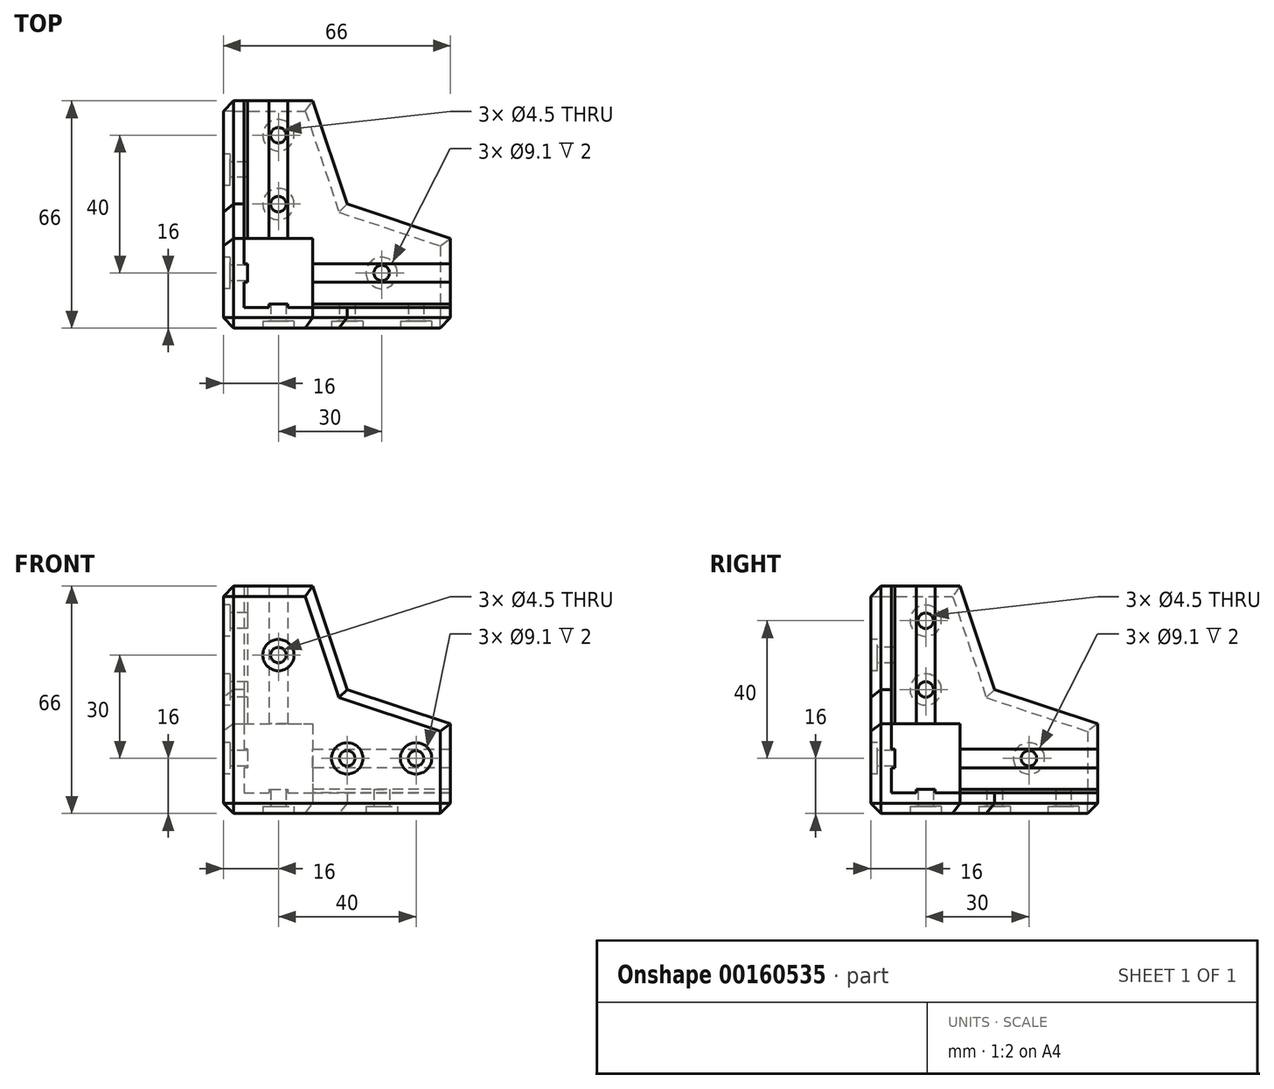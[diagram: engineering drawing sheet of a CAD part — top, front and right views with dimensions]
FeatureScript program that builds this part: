
annotation { "Feature Type Name" : "Feature", "Feature Type Description" : "" }
export const myFeature = defineFeature(function(context is Context, id is Id, definition is map)
    precondition{}
    {
        {
            var Q0;
            Q0=qCreatedBy(makeId("Top.planeOp"),FACE);
            var sketch = newSketch(context, id + "F0", { "sketchPlane" : qUnion([Q0])});
            skLineSegment(sketch, "E0", {"start": v(0, 0) * mm, "end": v(0, 66) * mm});
            skLineSegment(sketch, "E1", {"start": v(0, 66) * mm, "end": v(26, 66) * mm});
            skLineSegment(sketch, "E2", {"start": v(26, 66) * mm, "end": v(26, 26) * mm});
            skLineSegment(sketch, "E3", {"start": v(26, 26) * mm, "end": v(66, 26) * mm});
            skLineSegment(sketch, "E4", {"start": v(66, 26) * mm, "end": v(66, 0) * mm});
            skLineSegment(sketch, "E5", {"start": v(66, 0) * mm, "end": v(0, 0) * mm});
            skLineSegment(sketch, "E6", {"start": v(66, 6) * mm, "end": v(6, 6) * mm, "construction": true});
            skLineSegment(sketch, "E7", {"start": v(6, 6) * mm, "end": v(6, 66) * mm, "construction": true});
            skSolve(sketch);
        }
        {
            var Q0;
            Q0=qSketchRegion(id+"F0",true);
            extrude(context, id + "F1", {"entities" : qUnion([Q0]), "depth" : 6 * mm});
        }
        {
            var Q0;
            Q0=makeQuery(id+"F1.opExtrude","CAP_FACE",FACE,{"disambiguationData":[OSD([sQuery(id+"F0.wireOp",EDGE,"E0"),sQuery(id+"F0.wireOp",EDGE,"E1"),sQuery(id+"F0.wireOp",EDGE,"E2"),sQuery(id+"F0.wireOp",EDGE,"E3"),sQuery(id+"F0.wireOp",EDGE,"E4"),sQuery(id+"F0.wireOp",EDGE,"E5")])],"isStart":false});
            var sketch = newSketch(context, id + "F2", { "sketchPlane" : qUnion([Q0])});
            skLineSegment(sketch, "E8", {"start": v(0, 66) * mm, "end": v(6, 66) * mm});
            skLineSegment(sketch, "E9", {"start": v(6, 66) * mm, "end": v(6, 6) * mm});
            skLineSegment(sketch, "E10", {"start": v(6, 6) * mm, "end": v(66, 6) * mm});
            skLineSegment(sketch, "E11", {"start": v(66, 6) * mm, "end": v(66, 0) * mm});
            skLineSegment(sketch, "E12", {"start": v(66, 0) * mm, "end": v(0, 0) * mm});
            skLineSegment(sketch, "E13", {"start": v(0, 0) * mm, "end": v(0, 66) * mm});
            skSolve(sketch);
        }
        {
            var Q0;
            Q0=makeQuery(id+"F2.imprint","IMPRINT",FACE,{"disambiguationData":[TD([[makeQuery(id+"F2.imprint","IMPRINT",EDGE,{"derivedFrom":sQuery(id+"F2.wireOp",EDGE,"E8")}),-1.0]])]});
            extrude(context, id + "F3", {"entities" : qUnion([Q0]), "operationType" : NewBodyOperationType.ADD, "depth" : 20 * mm});
        }
        {
            var Q0;
            Q0=makeQuery(id+"F3.opExtrude","CAP_FACE",FACE,{"disambiguationData":[OSD([sQuery(id+"F2.wireOp",EDGE,"E8"),sQuery(id+"F2.wireOp",EDGE,"E9"),sQuery(id+"F2.wireOp",EDGE,"E10"),sQuery(id+"F2.wireOp",EDGE,"E11"),sQuery(id+"F2.wireOp",EDGE,"E12"),sQuery(id+"F2.wireOp",EDGE,"E13")])],"isStart":false});
            var sketch = newSketch(context, id + "F4", { "sketchPlane" : qUnion([Q0])});
            skLineSegment(sketch, "E14", {"start": v(6, 26) * mm, "end": v(0, 26) * mm});
            skLineSegment(sketch, "E15", {"start": v(0, 26) * mm, "end": v(0, 0) * mm});
            skLineSegment(sketch, "E16", {"start": v(0, 0) * mm, "end": v(26, 0) * mm});
            skLineSegment(sketch, "E17", {"start": v(26, 0) * mm, "end": v(26, 6) * mm});
            skLineSegment(sketch, "E18", {"start": v(26, 6) * mm, "end": v(6, 6) * mm});
            skLineSegment(sketch, "E19", {"start": v(6, 6) * mm, "end": v(6, 26) * mm});
            skSolve(sketch);
        }
        {
            var Q0;
            Q0=qSketchRegion(id+"F4",true);
            extrude(context, id + "F5", {"entities" : qUnion([Q0]), "operationType" : NewBodyOperationType.ADD, "depth" : 40 * mm});
        }
        {
            var Q0;
            Q0=makeQuery(id+"F1.opExtrude","CAP_FACE",FACE,{"disambiguationData":[OSD([sQuery(id+"F0.wireOp",EDGE,"E0"),sQuery(id+"F0.wireOp",EDGE,"E1"),sQuery(id+"F0.wireOp",EDGE,"E2"),sQuery(id+"F0.wireOp",EDGE,"E3"),sQuery(id+"F0.wireOp",EDGE,"E4"),sQuery(id+"F0.wireOp",EDGE,"E5")])],"isStart":false});
            var sketch = newSketch(context, id + "F6", { "sketchPlane" : qUnion([Q0])});
            skLineSegment(sketch, "E20", {"start": v(66, 16) * mm, "end": v(6, 16) * mm, "construction": true});
            skLineSegment(sketch, "E21", {"start": v(16, 66) * mm, "end": v(16, 6) * mm, "construction": true});
            skLineSegment(sketch, "E22", {"start": v(16, 6) * mm, "end": v(18.71, 6) * mm});
            skLineSegment(sketch, "E23", {"start": v(18.71, 6) * mm, "end": v(18.71, 7) * mm});
            skLineSegment(sketch, "E24", {"start": v(18.71, 7) * mm, "end": v(13.3, 7) * mm});
            skLineSegment(sketch, "E25", {"start": v(13.3, 7) * mm, "end": v(13.3, 6) * mm});
            skLineSegment(sketch, "E26", {"start": v(13.3, 6) * mm, "end": v(16, 6) * mm});
            skLineSegment(sketch, "E27", {"start": v(6, 16) * mm, "end": v(6, 18.7) * mm});
            skLineSegment(sketch, "E28", {"start": v(6, 18.7) * mm, "end": v(7, 18.7) * mm});
            skLineSegment(sketch, "E29", {"start": v(7, 18.7) * mm, "end": v(7, 13.29) * mm});
            skLineSegment(sketch, "E30", {"start": v(7, 13.29) * mm, "end": v(6, 13.29) * mm});
            skLineSegment(sketch, "E31", {"start": v(6, 13.29) * mm, "end": v(6, 16) * mm});
            skSolve(sketch);
        }
        {
            var Q0;
            Q0=qSketchRegion(id+"F6",true);
            extrude(context, id + "F7", {"entities" : qUnion([Q0]), "operationType" : NewBodyOperationType.ADD, "depth" : 60 * mm});
        }
        {
            var Q0;
            Q0=makeQuery(id+"F1.opExtrude","CAP_FACE",FACE,{"disambiguationData":[OSD([sQuery(id+"F0.wireOp",EDGE,"E0"),sQuery(id+"F0.wireOp",EDGE,"E1"),sQuery(id+"F0.wireOp",EDGE,"E2"),sQuery(id+"F0.wireOp",EDGE,"E3"),sQuery(id+"F0.wireOp",EDGE,"E4"),sQuery(id+"F0.wireOp",EDGE,"E5")])],"isStart":false});
            var sketch = newSketch(context, id + "F8", { "sketchPlane" : qUnion([Q0])});
            skLineSegment(sketch, "E32", {"start": v(66, 16) * mm, "end": v(7, 16) * mm, "construction": true});
            skLineSegment(sketch, "E33", {"start": v(66, 16) * mm, "end": v(66, 18.7) * mm});
            skLineSegment(sketch, "E34", {"start": v(66, 18.7) * mm, "end": v(26, 18.7) * mm});
            skLineSegment(sketch, "E35", {"start": v(26, 18.7) * mm, "end": v(26, 13.29) * mm});
            skLineSegment(sketch, "E36", {"start": v(26, 13.29) * mm, "end": v(66, 13.29) * mm});
            skLineSegment(sketch, "E37", {"start": v(66, 13.29) * mm, "end": v(66, 16) * mm});
            skLineSegment(sketch, "E38", {"start": v(16, 66) * mm, "end": v(16, 7) * mm, "construction": true});
            skLineSegment(sketch, "E39", {"start": v(16, 66) * mm, "end": v(13.3, 66) * mm});
            skLineSegment(sketch, "E40", {"start": v(13.3, 66) * mm, "end": v(13.3, 26) * mm});
            skLineSegment(sketch, "E41", {"start": v(13.3, 26) * mm, "end": v(18.7, 26) * mm});
            skLineSegment(sketch, "E42", {"start": v(18.7, 26) * mm, "end": v(18.7, 66) * mm});
            skLineSegment(sketch, "E43", {"start": v(18.7, 66) * mm, "end": v(16, 66) * mm});
            skSolve(sketch);
        }
        {
            var Q0;
            Q0=qSketchRegion(id+"F8",true);
            extrude(context, id + "F9", {"entities" : qUnion([Q0]), "operationType" : NewBodyOperationType.ADD, "flatOperationType" : FlatOperationType.REMOVE, "offsetDistance" : 25 * mm, "depth" : 1 * mm, "domain" : OperationDomain.MODEL});
        }
        {
            var Q0;
            {var subQ1=sQuery(id+"F2.wireOp",EDGE,"E10");var subQ2=sQuery(id+"F0.wireOp",EDGE,"E4");var subQ3=sQuery(id+"F4.wireOp",EDGE,"E18");Q0=makeQuery(id+"F7.boolean.opBoolean","SPLIT",FACE,{"disambiguationData":[TD([makeQuery(id+"F1.opExtrude","SWEPT_FACE",FACE,{"disambiguationData":[OSD([subQ2])]})])],"derivedFrom":makeQuery(id+"F5.boolean.opBoolean","MERGE",FACE,{"derivedFrom":[makeQuery(id+"F3.opExtrude","SWEPT_FACE",FACE,{"disambiguationData":[OSD([subQ1])]}),makeQuery(id+"F5.opExtrude","SWEPT_FACE",FACE,{"disambiguationData":[OSD([subQ3])]})]})});}
            var sketch = newSketch(context, id + "F10", { "sketchPlane" : qUnion([Q0])});
            skLineSegment(sketch, "E44", {"start": v(-66, 16) * mm, "end": v(-26, 16) * mm, "construction": true});
            skLineSegment(sketch, "E45", {"start": v(-66, 16) * mm, "end": v(-66, 13.3) * mm});
            skLineSegment(sketch, "E46", {"start": v(-66, 13.3) * mm, "end": v(-26, 13.3) * mm});
            skLineSegment(sketch, "E47", {"start": v(-26, 13.3) * mm, "end": v(-26, 16) * mm});
            skLineSegment(sketch, "E48", {"start": v(-26, 18.71) * mm, "end": v(-66, 18.71) * mm});
            skLineSegment(sketch, "E49", {"start": v(-66, 18.71) * mm, "end": v(-66, 16) * mm});
            skLineSegment(sketch, "E50", {"start": v(-26, 18.71) * mm, "end": v(-26, 16) * mm});
            skSolve(sketch);
        }
        {
            var Q0;
            Q0=qSketchRegion(id+"F10",true);
            extrude(context, id + "F11", {"entities" : qUnion([Q0]), "operationType" : NewBodyOperationType.ADD, "flatOperationType" : FlatOperationType.REMOVE, "offsetDistance" : 25 * mm, "depth" : 1 * mm, "domain" : OperationDomain.MODEL});
        }
        {
            var Q0;
            {var subQ0=sQuery(id+"F2.wireOp",EDGE,"E9");var subQ3=sQuery(id+"F0.wireOp",EDGE,"E1");var subQ5=sQuery(id+"F4.wireOp",EDGE,"E19");Q0=makeQuery(id+"F7.boolean.opBoolean","SPLIT",FACE,{"disambiguationData":[TD([makeQuery(id+"F1.opExtrude","SWEPT_FACE",FACE,{"disambiguationData":[OSD([subQ3])]})])],"derivedFrom":makeQuery(id+"F5.boolean.opBoolean","MERGE",FACE,{"derivedFrom":[makeQuery(id+"F3.opExtrude","SWEPT_FACE",FACE,{"disambiguationData":[OSD([subQ0])]}),makeQuery(id+"F5.opExtrude","SWEPT_FACE",FACE,{"disambiguationData":[OSD([subQ5])]})]})});}
            var sketch = newSketch(context, id + "F12", { "sketchPlane" : qUnion([Q0])});
            skLineSegment(sketch, "E51", {"start": v(66, 16) * mm, "end": v(26, 16) * mm, "construction": true});
            skLineSegment(sketch, "E52", {"start": v(66, 16) * mm, "end": v(66, 18.71) * mm});
            skLineSegment(sketch, "E53", {"start": v(66, 18.71) * mm, "end": v(26, 18.7) * mm});
            skLineSegment(sketch, "E54", {"start": v(26, 18.7) * mm, "end": v(26, 13.29) * mm});
            skLineSegment(sketch, "E55", {"start": v(26, 13.29) * mm, "end": v(66, 13.29) * mm});
            skLineSegment(sketch, "E56", {"start": v(66, 16) * mm, "end": v(66, 13.29) * mm});
            skSolve(sketch);
        }
        {
            var Q0;
            Q0=qSketchRegion(id+"F12",true);
            extrude(context, id + "F13", {"entities" : qUnion([Q0]), "operationType" : NewBodyOperationType.ADD, "flatOperationType" : FlatOperationType.REMOVE, "offsetDistance" : 25 * mm, "depth" : 1 * mm, "domain" : OperationDomain.MODEL});
        }
        {
            var Q0;
            Q0=makeQuery(id+"F5.boolean.opBoolean","MERGE",FACE,{"derivedFrom":[makeQuery(id+"F3.boolean.opBoolean","MERGE",FACE,{"derivedFrom":[makeQuery(id+"F1.opExtrude","SWEPT_FACE",FACE,{"disambiguationData":[OSD([sQuery(id+"F0.wireOp",EDGE,"E5")])]}),makeQuery(id+"F3.opExtrude","SWEPT_FACE",FACE,{"disambiguationData":[OSD([sQuery(id+"F2.wireOp",EDGE,"E12")])]})]}),makeQuery(id+"F5.opExtrude","SWEPT_FACE",FACE,{"disambiguationData":[OSD([sQuery(id+"F4.wireOp",EDGE,"E16")])]})]});
            var sketch = newSketch(context, id + "F14", { "sketchPlane" : qUnion([Q0])});
            skLineSegment(sketch, "E57", {"start": v(6, 66) * mm, "end": v(6, 6) * mm, "construction": true});
            skLineSegment(sketch, "E58", {"start": v(6, 6) * mm, "end": v(66, 6) * mm, "construction": true});
            skCircle(sketch, "E59", {"center": v(56, 16) * mm, "radius": 2.25 * mm});
            skCircle(sketch, "E60", {"center": v(36, 16) * mm, "radius": 2.25 * mm});
            skCircle(sketch, "E61", {"center": v(16, 46) * mm, "radius": 2.25 * mm});
            skLineSegment(sketch, "E62", {"start": v(26, 26) * mm, "end": v(6, 26) * mm, "construction": true});
            skLineSegment(sketch, "E63", {"start": v(26, 26) * mm, "end": v(26, 6) * mm, "construction": true});
            skSolve(sketch);
        }
        {
            var Q0;
            Q0=makeQuery(id+"F14.imprint","IMPRINT",FACE,{"disambiguationData":[TD([[makeQuery(id+"F14.imprint","IMPRINT",EDGE,{"derivedFrom":sQuery(id+"F14.wireOp",EDGE,"E59")}),1.0]])]});
            var Q1;
            Q1=makeQuery(id+"F14.imprint","IMPRINT",FACE,{"disambiguationData":[TD([[makeQuery(id+"F14.imprint","IMPRINT",EDGE,{"derivedFrom":sQuery(id+"F14.wireOp",EDGE,"E61")}),1.0]])]});
            var Q2;
            Q2=makeQuery(id+"F14.imprint","IMPRINT",FACE,{"disambiguationData":[TD([[makeQuery(id+"F14.imprint","IMPRINT",EDGE,{"derivedFrom":sQuery(id+"F14.wireOp",EDGE,"E60")}),1.0]])]});
            extrude(context, id + "F15", {"entities" : qUnion([Q0, Q1, Q2]), "operationType" : NewBodyOperationType.REMOVE, "endBound" : BoundingType.UP_TO_NEXT, "oppositeDirection" : true, "depth" : 25 * mm});
        }
        {
            var Q0;
            Q0=makeQuery(id+"F5.boolean.opBoolean","MERGE",FACE,{"derivedFrom":[makeQuery(id+"F3.boolean.opBoolean","MERGE",FACE,{"derivedFrom":[makeQuery(id+"F1.opExtrude","SWEPT_FACE",FACE,{"disambiguationData":[OSD([sQuery(id+"F0.wireOp",EDGE,"E0")])]}),makeQuery(id+"F3.opExtrude","SWEPT_FACE",FACE,{"disambiguationData":[OSD([sQuery(id+"F2.wireOp",EDGE,"E13")])]})]}),makeQuery(id+"F5.opExtrude","SWEPT_FACE",FACE,{"disambiguationData":[OSD([sQuery(id+"F4.wireOp",EDGE,"E15")])]})]});
            var sketch = newSketch(context, id + "F16", { "sketchPlane" : qUnion([Q0])});
            skLineSegment(sketch, "E64", {"start": v(-6, 66) * mm, "end": v(-6, 6) * mm, "construction": true});
            skLineSegment(sketch, "E65", {"start": v(-6, 6) * mm, "end": v(-66, 6) * mm, "construction": true});
            skCircle(sketch, "E66", {"center": v(-16, 56) * mm, "radius": 2.25 * mm});
            skCircle(sketch, "E67", {"center": v(-46, 16) * mm, "radius": 2.25 * mm});
            skCircle(sketch, "E68", {"center": v(-16, 36) * mm, "radius": 2.25 * mm});
            skSolve(sketch);
        }
        {
            var Q0;
            Q0=qSketchRegion(id+"F16",true);
            extrude(context, id + "F17", {"entities" : qUnion([Q0]), "operationType" : NewBodyOperationType.REMOVE, "endBound" : BoundingType.UP_TO_NEXT, "oppositeDirection" : true, "depth" : 25 * mm});
        }
        {
            var Q0;
            Q0=makeQuery(id+"F1.opExtrude","CAP_FACE",FACE,{"disambiguationData":[OSD([sQuery(id+"F0.wireOp",EDGE,"E0"),sQuery(id+"F0.wireOp",EDGE,"E1"),sQuery(id+"F0.wireOp",EDGE,"E2"),sQuery(id+"F0.wireOp",EDGE,"E3"),sQuery(id+"F0.wireOp",EDGE,"E4"),sQuery(id+"F0.wireOp",EDGE,"E5")])],"isStart":true});
            var sketch = newSketch(context, id + "F18", { "sketchPlane" : qUnion([Q0])});
            skLineSegment(sketch, "E69", {"start": v(66, -6) * mm, "end": v(6, -6) * mm, "construction": true});
            skLineSegment(sketch, "E70", {"start": v(6, -6) * mm, "end": v(6, -66) * mm, "construction": true});
            skCircle(sketch, "E71", {"center": v(46, -16) * mm, "radius": 2.25 * mm});
            skCircle(sketch, "E72", {"center": v(16, -56) * mm, "radius": 2.25 * mm});
            skCircle(sketch, "E73", {"center": v(16, -36) * mm, "radius": 2.25 * mm});
            skSolve(sketch);
        }
        {
            var Q0;
            Q0=qSketchRegion(id+"F18",true);
            extrude(context, id + "F19", {"entities" : qUnion([Q0]), "operationType" : NewBodyOperationType.REMOVE, "endBound" : BoundingType.UP_TO_NEXT, "oppositeDirection" : true, "depth" : 25 * mm});
        }
        {
            var Q0;
            Q0=makeQuery(id+"F5.boolean.opBoolean","MERGE",FACE,{"derivedFrom":[makeQuery(id+"F3.boolean.opBoolean","MERGE",FACE,{"derivedFrom":[makeQuery(id+"F1.opExtrude","SWEPT_FACE",FACE,{"disambiguationData":[OSD([sQuery(id+"F0.wireOp",EDGE,"E5")])]}),makeQuery(id+"F3.opExtrude","SWEPT_FACE",FACE,{"disambiguationData":[OSD([sQuery(id+"F2.wireOp",EDGE,"E12")])]})]}),makeQuery(id+"F5.opExtrude","SWEPT_FACE",FACE,{"disambiguationData":[OSD([sQuery(id+"F4.wireOp",EDGE,"E16")])]})]});
            var sketch = newSketch(context, id + "F20", { "sketchPlane" : qUnion([Q0])});
            skCircle(sketch, "E74", {"center": v(16, 46) * mm, "radius": 4.55 * mm});
            skCircle(sketch, "E75", {"center": v(36, 16) * mm, "radius": 4.55 * mm});
            skCircle(sketch, "E76", {"center": v(56, 16) * mm, "radius": 4.55 * mm});
            skSolve(sketch);
        }
        {
            var Q0;
            Q0=qSketchRegion(id+"F20",true);
            extrude(context, id + "F21", {"entities" : qUnion([Q0]), "operationType" : NewBodyOperationType.REMOVE, "oppositeDirection" : true, "depth" : 2 * mm});
        }
        {
            var Q0;
            Q0=makeQuery(id+"F5.boolean.opBoolean","MERGE",FACE,{"derivedFrom":[makeQuery(id+"F3.boolean.opBoolean","MERGE",FACE,{"derivedFrom":[makeQuery(id+"F1.opExtrude","SWEPT_FACE",FACE,{"disambiguationData":[OSD([sQuery(id+"F0.wireOp",EDGE,"E0")])]}),makeQuery(id+"F3.opExtrude","SWEPT_FACE",FACE,{"disambiguationData":[OSD([sQuery(id+"F2.wireOp",EDGE,"E13")])]})]}),makeQuery(id+"F5.opExtrude","SWEPT_FACE",FACE,{"disambiguationData":[OSD([sQuery(id+"F4.wireOp",EDGE,"E15")])]})]});
            var sketch = newSketch(context, id + "F22", { "sketchPlane" : qUnion([Q0])});
            skCircle(sketch, "E77", {"center": v(-16, 56) * mm, "radius": 4.55 * mm});
            skCircle(sketch, "E78", {"center": v(-46, 16) * mm, "radius": 4.55 * mm});
            skCircle(sketch, "E79", {"center": v(-16, 36) * mm, "radius": 4.55 * mm});
            skSolve(sketch);
        }
        {
            var Q0;
            Q0=qSketchRegion(id+"F22",true);
            extrude(context, id + "F23", {"entities" : qUnion([Q0]), "operationType" : NewBodyOperationType.REMOVE, "oppositeDirection" : true, "depth" : 2 * mm});
        }
        {
            var Q0;
            Q0=makeQuery(id+"F1.opExtrude","CAP_FACE",FACE,{"disambiguationData":[OSD([sQuery(id+"F0.wireOp",EDGE,"E0"),sQuery(id+"F0.wireOp",EDGE,"E1"),sQuery(id+"F0.wireOp",EDGE,"E2"),sQuery(id+"F0.wireOp",EDGE,"E3"),sQuery(id+"F0.wireOp",EDGE,"E4"),sQuery(id+"F0.wireOp",EDGE,"E5")])],"isStart":true});
            var sketch = newSketch(context, id + "F24", { "sketchPlane" : qUnion([Q0])});
            skCircle(sketch, "E80", {"center": v(16, -56) * mm, "radius": 4.55 * mm});
            skCircle(sketch, "E81", {"center": v(46, -16) * mm, "radius": 4.55 * mm});
            skCircle(sketch, "E82", {"center": v(16, -36) * mm, "radius": 4.55 * mm});
            skSolve(sketch);
        }
        {
            var Q0;
            Q0=qSketchRegion(id+"F24",true);
            extrude(context, id + "F25", {"entities" : qUnion([Q0]), "operationType" : NewBodyOperationType.REMOVE, "oppositeDirection" : true, "depth" : 2 * mm});
        }
        {
            var Q0;
            Q0=makeQuery(id+"F1.opExtrude","CAP_FACE",FACE,{"disambiguationData":[OSD([sQuery(id+"F0.wireOp",EDGE,"E0"),sQuery(id+"F0.wireOp",EDGE,"E1"),sQuery(id+"F0.wireOp",EDGE,"E2"),sQuery(id+"F0.wireOp",EDGE,"E3"),sQuery(id+"F0.wireOp",EDGE,"E4"),sQuery(id+"F0.wireOp",EDGE,"E5")])],"isStart":false});
            var sketch = newSketch(context, id + "F26", { "sketchPlane" : qUnion([Q0])});
            skLineSegment(sketch, "E83.bottom", {"start": v(6, 6) * mm, "end": v(26, 6) * mm});
            skLineSegment(sketch, "E83.top", {"start": v(6, 26) * mm, "end": v(26, 26) * mm});
            skLineSegment(sketch, "E83.left", {"start": v(6, 6) * mm, "end": v(6, 26) * mm});
            skLineSegment(sketch, "E83.right", {"start": v(26, 6) * mm, "end": v(26, 26) * mm});
            skSolve(sketch);
        }
        {
            var Q0;
            Q0=qSketchRegion(id+"F26",true);
            extrude(context, id + "F27", {"entities" : qUnion([Q0]), "operationType" : NewBodyOperationType.ADD, "depth" : 20 * mm});
        }
        {
            var Q0;
            Q0=makeQuery(id+"F5.boolean.opBoolean","MERGE",FACE,{"derivedFrom":[makeQuery(id+"F3.boolean.opBoolean","MERGE",FACE,{"derivedFrom":[makeQuery(id+"F1.opExtrude","SWEPT_FACE",FACE,{"disambiguationData":[OSD([sQuery(id+"F0.wireOp",EDGE,"E5")])]}),makeQuery(id+"F3.opExtrude","SWEPT_FACE",FACE,{"disambiguationData":[OSD([sQuery(id+"F2.wireOp",EDGE,"E12")])]})]}),makeQuery(id+"F5.opExtrude","SWEPT_FACE",FACE,{"disambiguationData":[OSD([sQuery(id+"F4.wireOp",EDGE,"E16")])]})]});
            var sketch = newSketch(context, id + "F28", { "sketchPlane" : qUnion([Q0])});
            skLineSegment(sketch, "E84", {"start": v(26, 36) * mm, "end": v(36, 36) * mm, "construction": true});
            skLineSegment(sketch, "E85", {"start": v(36, 36) * mm, "end": v(36, 26) * mm, "construction": true});
            skLineSegment(sketch, "E86", {"start": v(26, 66) * mm, "end": v(36, 36) * mm});
            skLineSegment(sketch, "E87", {"start": v(36, 36) * mm, "end": v(66, 26) * mm});
            skLineSegment(sketch, "E88", {"start": v(66, 26) * mm, "end": v(26, 26) * mm});
            skLineSegment(sketch, "E89", {"start": v(26, 26) * mm, "end": v(26, 66) * mm});
            skSolve(sketch);
        }
        {
            var Q0;
            Q0 = qSketchRegion(id + "F28", true);
            extrude(context, id + "F29", {"entities" : qUnion([Q0]), "operationType" : NewBodyOperationType.ADD, "oppositeDirection" : true, "depth" : 6 * mm});
        }
        {
            var Q0;
            Q0=makeQuery(id+"F5.boolean.opBoolean","MERGE",FACE,{"derivedFrom":[makeQuery(id+"F3.boolean.opBoolean","MERGE",FACE,{"derivedFrom":[makeQuery(id+"F1.opExtrude","SWEPT_FACE",FACE,{"disambiguationData":[OSD([sQuery(id+"F0.wireOp",EDGE,"E0")])]}),makeQuery(id+"F3.opExtrude","SWEPT_FACE",FACE,{"disambiguationData":[OSD([sQuery(id+"F2.wireOp",EDGE,"E13")])]})]}),makeQuery(id+"F5.opExtrude","SWEPT_FACE",FACE,{"disambiguationData":[OSD([sQuery(id+"F4.wireOp",EDGE,"E15")])]})]});
            var sketch = newSketch(context, id + "F30", { "sketchPlane" : qUnion([Q0])});
            skLineSegment(sketch, "E90", {"start": v(-26, 36) * mm, "end": v(-36, 36) * mm, "construction": true});
            skLineSegment(sketch, "E91", {"start": v(-36, 36) * mm, "end": v(-36, 26) * mm, "construction": true});
            skLineSegment(sketch, "E92", {"start": v(-26, 66) * mm, "end": v(-36, 36) * mm});
            skLineSegment(sketch, "E93", {"start": v(-36, 36) * mm, "end": v(-66, 26) * mm});
            skLineSegment(sketch, "E94", {"start": v(-66, 26) * mm, "end": v(-26, 26) * mm});
            skLineSegment(sketch, "E95", {"start": v(-26, 26) * mm, "end": v(-26, 66) * mm});
            skSolve(sketch);
        }
        {
            var Q0;
            Q0 = qSketchRegion(id + "F30", true);
            extrude(context, id + "F31", {"entities" : qUnion([Q0]), "operationType" : NewBodyOperationType.ADD, "oppositeDirection" : true, "depth" : 6 * mm});
        }
        {
            var Q0;
            Q0=makeQuery(id+"F1.opExtrude","CAP_FACE",FACE,{"disambiguationData":[OSD([sQuery(id+"F0.wireOp",EDGE,"E0"),sQuery(id+"F0.wireOp",EDGE,"E1"),sQuery(id+"F0.wireOp",EDGE,"E2"),sQuery(id+"F0.wireOp",EDGE,"E3"),sQuery(id+"F0.wireOp",EDGE,"E4"),sQuery(id+"F0.wireOp",EDGE,"E5")])],"isStart":true});
            var sketch = newSketch(context, id + "F32", { "sketchPlane" : qUnion([Q0])});
            skLineSegment(sketch, "E96", {"start": v(36, -26) * mm, "end": v(36, -36) * mm, "construction": true});
            skLineSegment(sketch, "E97", {"start": v(36, -36) * mm, "end": v(26, -36) * mm, "construction": true});
            skLineSegment(sketch, "E98", {"start": v(66, -26) * mm, "end": v(36, -36) * mm});
            skLineSegment(sketch, "E99", {"start": v(36, -36) * mm, "end": v(26, -66) * mm});
            skLineSegment(sketch, "E100", {"start": v(26, -66) * mm, "end": v(26, -26) * mm});
            skLineSegment(sketch, "E101", {"start": v(26, -26) * mm, "end": v(66, -26) * mm});
            skSolve(sketch);
        }
        {
            var Q0;
            Q0 = qSketchRegion(id + "F32", true);
            extrude(context, id + "F33", {"entities" : qUnion([Q0]), "operationType" : NewBodyOperationType.ADD, "oppositeDirection" : true, "depth" : 6 * mm});
        }
        {
            var Q0;
            Q0=makeQuery(id+"F1.opExtrude","CAP_EDGE",EDGE,{"disambiguationData":[OSD([sQuery(id+"F0.wireOp",EDGE,"E5")])],"isStart":true});
            var Q1;
            Q1=makeQuery(id+"F1.opExtrude","CAP_EDGE",EDGE,{"disambiguationData":[OSD([sQuery(id+"F0.wireOp",EDGE,"E4")])],"isStart":true});
            var Q2;
            Q2=makeQuery(id+"F33.opExtrude","CAP_EDGE",EDGE,{"disambiguationData":[OSD([sQuery(id+"F32.wireOp",EDGE,"E98")])],"isStart":true});
            var Q3;
            Q3=makeQuery(id+"F33.opExtrude","CAP_EDGE",EDGE,{"disambiguationData":[OSD([sQuery(id+"F32.wireOp",EDGE,"E99")])],"isStart":true});
            var Q4;
            Q4=makeQuery(id+"F1.opExtrude","CAP_EDGE",EDGE,{"disambiguationData":[OSD([sQuery(id+"F0.wireOp",EDGE,"E1")])],"isStart":true});
            var Q5;
            Q5=makeQuery(id+"F1.opExtrude","CAP_EDGE",EDGE,{"disambiguationData":[OSD([sQuery(id+"F0.wireOp",EDGE,"E0")])],"isStart":true});
            var Q6;
            Q6=makeQuery(id+"F3.boolean.opBoolean","MERGE",EDGE,{"derivedFrom":[makeQuery(id+"F1.opExtrude","SWEPT_EDGE",EDGE,{"disambiguationData":[OSD([sQuery(id+"F0.wireOp",EDGE,"E0"),sQuery(id+"F0.wireOp",EDGE,"E1")])]}),makeQuery(id+"F3.opExtrude","SWEPT_EDGE",EDGE,{"disambiguationData":[OSD([sQuery(id+"F2.wireOp",EDGE,"E8"),sQuery(id+"F2.wireOp",EDGE,"E13")])]})]});
            var Q7;
            Q7=makeQuery(id+"F31.opExtrude","CAP_EDGE",EDGE,{"disambiguationData":[OSD([sQuery(id+"F30.wireOp",EDGE,"E93")])],"isStart":true});
            var Q8;
            Q8=makeQuery(id+"F31.opExtrude","CAP_EDGE",EDGE,{"disambiguationData":[OSD([sQuery(id+"F30.wireOp",EDGE,"E92")])],"isStart":true});
            var Q9;
            Q9=makeQuery(id+"F5.opExtrude","CAP_EDGE",EDGE,{"disambiguationData":[OSD([sQuery(id+"F4.wireOp",EDGE,"E15")])],"isStart":false});
            var Q10;
            Q10=makeQuery(id+"F5.boolean.opBoolean","MERGE",EDGE,{"derivedFrom":[makeQuery(id+"F3.boolean.opBoolean","MERGE",EDGE,{"derivedFrom":[makeQuery(id+"F1.opExtrude","SWEPT_EDGE",EDGE,{"disambiguationData":[OSD([sQuery(id+"F0.wireOp",EDGE,"E0"),sQuery(id+"F0.wireOp",EDGE,"E5")])]}),makeQuery(id+"F3.opExtrude","SWEPT_EDGE",EDGE,{"disambiguationData":[OSD([sQuery(id+"F2.wireOp",EDGE,"E12"),sQuery(id+"F2.wireOp",EDGE,"E13")])]})]}),makeQuery(id+"F5.opExtrude","SWEPT_EDGE",EDGE,{"disambiguationData":[OSD([sQuery(id+"F4.wireOp",EDGE,"E15"),sQuery(id+"F4.wireOp",EDGE,"E16")])]})]});
            var Q11;
            Q11=makeQuery(id+"F3.boolean.opBoolean","MERGE",EDGE,{"derivedFrom":[makeQuery(id+"F1.opExtrude","SWEPT_EDGE",EDGE,{"disambiguationData":[OSD([sQuery(id+"F0.wireOp",EDGE,"E4"),sQuery(id+"F0.wireOp",EDGE,"E5")])]}),makeQuery(id+"F3.opExtrude","SWEPT_EDGE",EDGE,{"disambiguationData":[OSD([sQuery(id+"F2.wireOp",EDGE,"E11"),sQuery(id+"F2.wireOp",EDGE,"E12")])]})]});
            var Q12;
            Q12=makeQuery(id+"F29.opExtrude","CAP_EDGE",EDGE,{"disambiguationData":[OSD([sQuery(id+"F28.wireOp",EDGE,"E87")])],"isStart":true});
            var Q13;
            Q13=makeQuery(id+"F29.opExtrude","CAP_EDGE",EDGE,{"disambiguationData":[OSD([sQuery(id+"F28.wireOp",EDGE,"E86")])],"isStart":true});
            var Q14;
            Q14=makeQuery(id+"F5.opExtrude","CAP_EDGE",EDGE,{"disambiguationData":[OSD([sQuery(id+"F4.wireOp",EDGE,"E16")])],"isStart":false});
            chamfer(context, id + "F34", {"entities" : qUnion([Q0, Q1, Q2, Q3, Q4, Q5, Q6, Q7, Q8, Q9, Q10, Q11, Q12, Q13, Q14]), "width" : 3 * mm, "tangentPropagation" : true});
        }
    });
